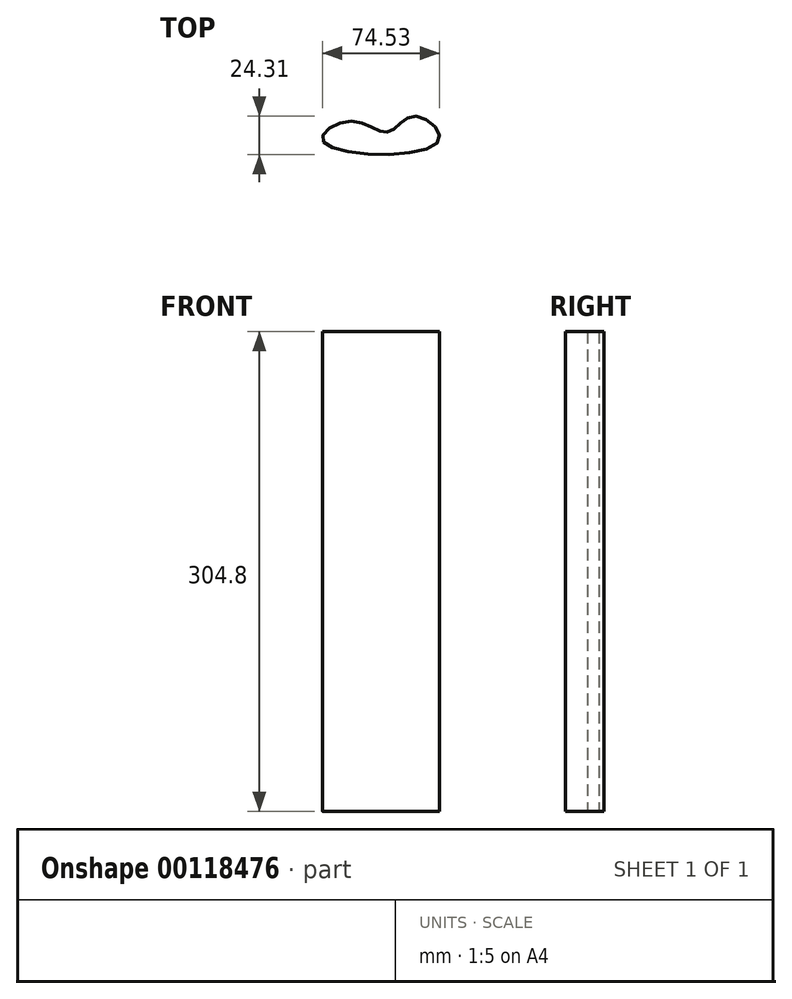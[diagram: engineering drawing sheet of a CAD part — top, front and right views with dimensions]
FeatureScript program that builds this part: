
annotation { "Feature Type Name" : "Feature", "Feature Type Description" : "" }
export const myFeature = defineFeature(function(context is Context, id is Id, definition is map)
    precondition{}
    {
        {
            var Q0;
            Q0=qCreatedBy(makeId("Top.planeOp"),FACE);
            var sketch = newSketch(context, id + "F0", { "sketchPlane" : qUnion([Q0])});
            skFitSpline(sketch, "E0", {"points": [v(0, 0) * mm, v(17.13, 13.21) * mm, v(40.95, 6.24) * mm, v(58.08, 16.4) * mm, v(72.9, 0) * mm, v(0, 0) * mm]});
            skSolve(sketch);
        }
        {
            var Q0;
            Q0 = qSketchRegion(id + "F0", true);
            extrude(context, id + "F1", {"entities" : qUnion([Q0]), "depth" : 304.8 * mm});
        }
    });
